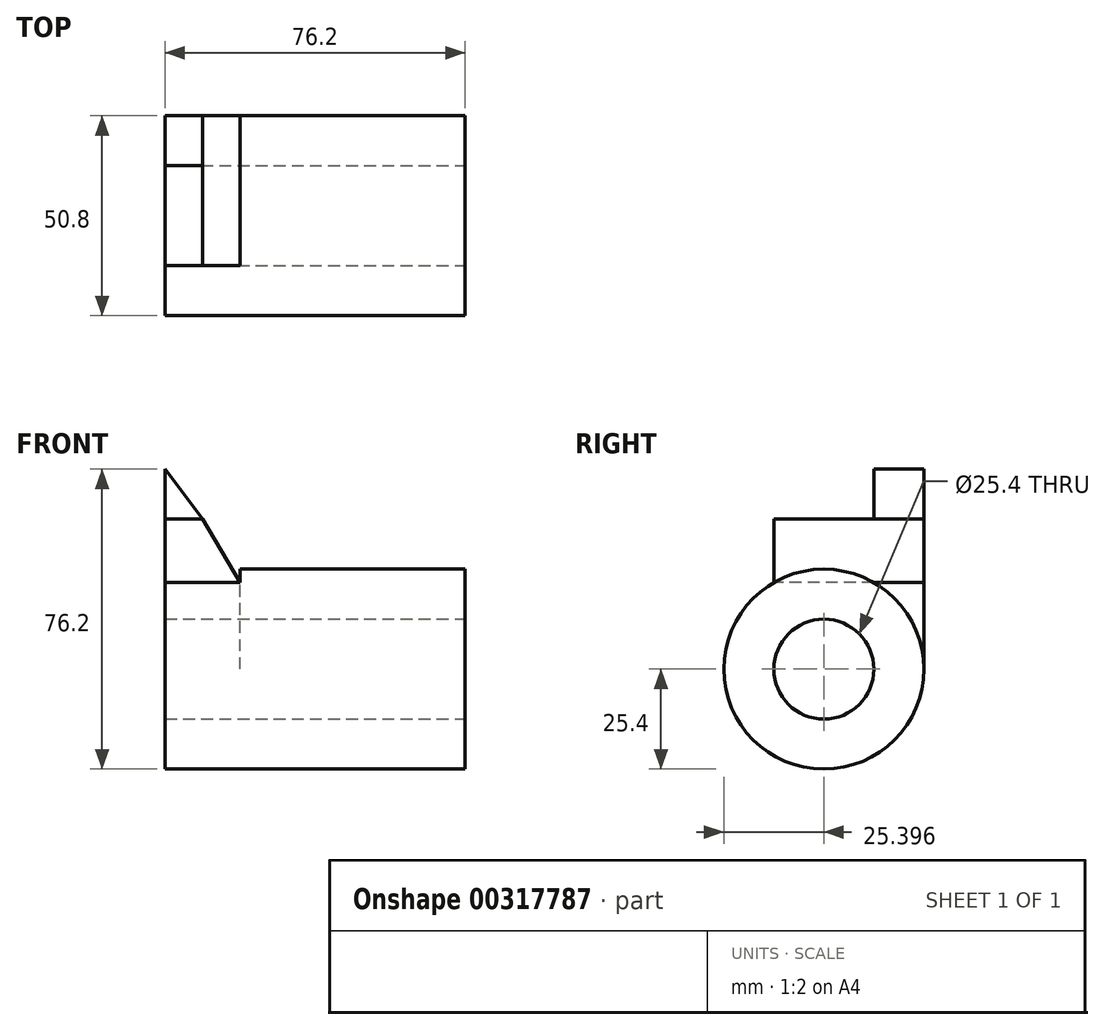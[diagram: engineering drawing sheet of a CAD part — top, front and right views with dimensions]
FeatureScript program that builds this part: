
annotation { "Feature Type Name" : "Feature", "Feature Type Description" : "" }
export const myFeature = defineFeature(function(context is Context, id is Id, definition is map)
    precondition{}
    {
        {
            var Q0;
            Q0=qCreatedBy(makeId("Right.planeOp"),FACE);
            var sketch = newSketch(context, id + "F0", { "sketchPlane" : qUnion([Q0])});
            skCircle(sketch, "E0", {"center": v(18.89, -18.47) * mm, "radius": 25.4 * mm});
            skCircle(sketch, "E1", {"center": v(18.89, -18.47) * mm, "radius": 12.7 * mm});
            skLineSegment(sketch, "E2", {"start": v(27.29, -8.95) * mm, "end": v(42.43, -8.95) * mm});
            skLineSegment(sketch, "E3", {"start": v(10.49, -8.95) * mm, "end": v(-4.66, -8.95) * mm});
            skPoint(sketch, "E4.orphan", {"position": v(18.89, 6.93) * mm});
            skLineSegment(sketch, "E5", {"start": v(44.29, -18.47) * mm, "end": v(44.29, 32.33) * mm});
            skLineSegment(sketch, "E6", {"start": v(44.29, 32.33) * mm, "end": v(31.59, 32.33) * mm});
            skLineSegment(sketch, "E7", {"start": v(31.59, 32.33) * mm, "end": v(31.59, 19.63) * mm});
            skLineSegment(sketch, "E8", {"start": v(31.59, 19.63) * mm, "end": v(6.19, 19.63) * mm});
            skLineSegment(sketch, "E9", {"start": v(6.19, 19.63) * mm, "end": v(6.19, 3.53) * mm});
            skSolve(sketch);
        }
        {
            var Q0;
            {var subQ0=sQuery(id+"F0.wireOp",EDGE,"E2");Q0=makeQuery(id+"F0.imprint","IMPRINT",FACE,{"disambiguationData":[TD([[makeQuery(id+"F0.imprint","IMPRINT",EDGE,{"derivedFrom":subQ0}),1.0]])]});}
            var Q1;
            {var subQ0=sQuery(id+"F0.wireOp",EDGE,"E2");Q1=makeQuery(id+"F0.imprint","IMPRINT",FACE,{"disambiguationData":[TD([[makeQuery(id+"F0.imprint","IMPRINT",EDGE,{"derivedFrom":subQ0}),-1.0]])]});}
            extrude(context, id + "F1", {"entities" : qUnion([Q0, Q1]), "oppositeDirection" : true, "depth" : 76.2 * mm});
        }
        {
            var Q0;
            {var subQ0=sQuery(id+"F0.wireOp",EDGE,"E5");Q0=makeQuery(id+"F0.imprint","IMPRINT",FACE,{"disambiguationData":[TD([[makeQuery(id+"F0.imprint","IMPRINT",EDGE,{"derivedFrom":subQ0}),1.0]])]});}
            extrude(context, id + "F2", {"entities" : qUnion([Q0]), "operationType" : NewBodyOperationType.ADD, "oppositeDirection" : true, "depth" : 76.2 * mm});
        }
        {
            var Q0;
            {var subQ0=sQuery(id+"F0.wireOp",EDGE,"E5");Q0=makeQuery(id+"F0.imprint","IMPRINT",FACE,{"disambiguationData":[TD([[makeQuery(id+"F0.imprint","IMPRINT",EDGE,{"derivedFrom":subQ0}),1.0]])]});}
            extrude(context, id + "F3", {"entities" : qUnion([Q0]), "operationType" : NewBodyOperationType.REMOVE, "oppositeDirection" : true, "depth" : 57.15 * mm});
        }
        {
            var Q0;
            Q0=makeQuery(id+"F2.opExtrude","SWEPT_FACE",FACE,{"disambiguationData":[OSD([sQuery(id+"F0.wireOp",EDGE,"E7")])]});
            var sketch = newSketch(context, id + "F4", { "sketchPlane" : qUnion([Q0])});
            skLineSegment(sketch, "E10", {"start": v(-76.2, 19.63) * mm, "end": v(-66.67, 19.63) * mm});
            skLineSegment(sketch, "E11", {"start": v(-66.67, 19.63) * mm, "end": v(-76.2, 32.33) * mm});
            skLineSegment(sketch, "E12", {"start": v(-76.2, 32.33) * mm, "end": v(-57.15, 32.33) * mm});
            skLineSegment(sketch, "E13", {"start": v(-57.15, 32.33) * mm, "end": v(-57.15, 19.63) * mm});
            skLineSegment(sketch, "E14", {"start": v(-57.15, 19.63) * mm, "end": v(-66.67, 19.63) * mm});
            skSolve(sketch);
        }
        {
            var Q0;
            Q0=makeQuery(id+"F4.imprint","IMPRINT",FACE,{"disambiguationData":[TD([[makeQuery(id+"F4.imprint","IMPRINT",EDGE,{"derivedFrom":sQuery(id+"F4.wireOp",EDGE,"E11")}),-1.0]])]});
            extrude(context, id + "F5", {"entities" : qUnion([Q0]), "operationType" : NewBodyOperationType.REMOVE, "oppositeDirection" : true, "depth" : 25.4 * mm});
        }
        {
            var Q0;
            Q0=makeQuery(id+"F2.opExtrude","SWEPT_FACE",FACE,{"disambiguationData":[OSD([sQuery(id+"F0.wireOp",EDGE,"E9")])]});
            var sketch = newSketch(context, id + "F6", { "sketchPlane" : qUnion([Q0])});
            skLineSegment(sketch, "E15", {"start": v(-66.68, 19.63) * mm, "end": v(-57.15, 3.53) * mm});
            skLineSegment(sketch, "E16", {"start": v(-57.15, 3.53) * mm, "end": v(-57.15, 19.63) * mm});
            skLineSegment(sketch, "E17", {"start": v(-57.15, 19.63) * mm, "end": v(-66.68, 19.63) * mm});
            skSolve(sketch);
        }
        {
            var Q0;
            Q0=makeQuery(id+"F6.imprint","IMPRINT",FACE,{"disambiguationData":[TD([[makeQuery(id+"F6.imprint","IMPRINT",EDGE,{"derivedFrom":sQuery(id+"F6.wireOp",EDGE,"E15")}),1.0]])]});
            extrude(context, id + "F7", {"entities" : qUnion([Q0]), "operationType" : NewBodyOperationType.REMOVE, "oppositeDirection" : true, "depth" : 76.2 * mm});
        }
    });
